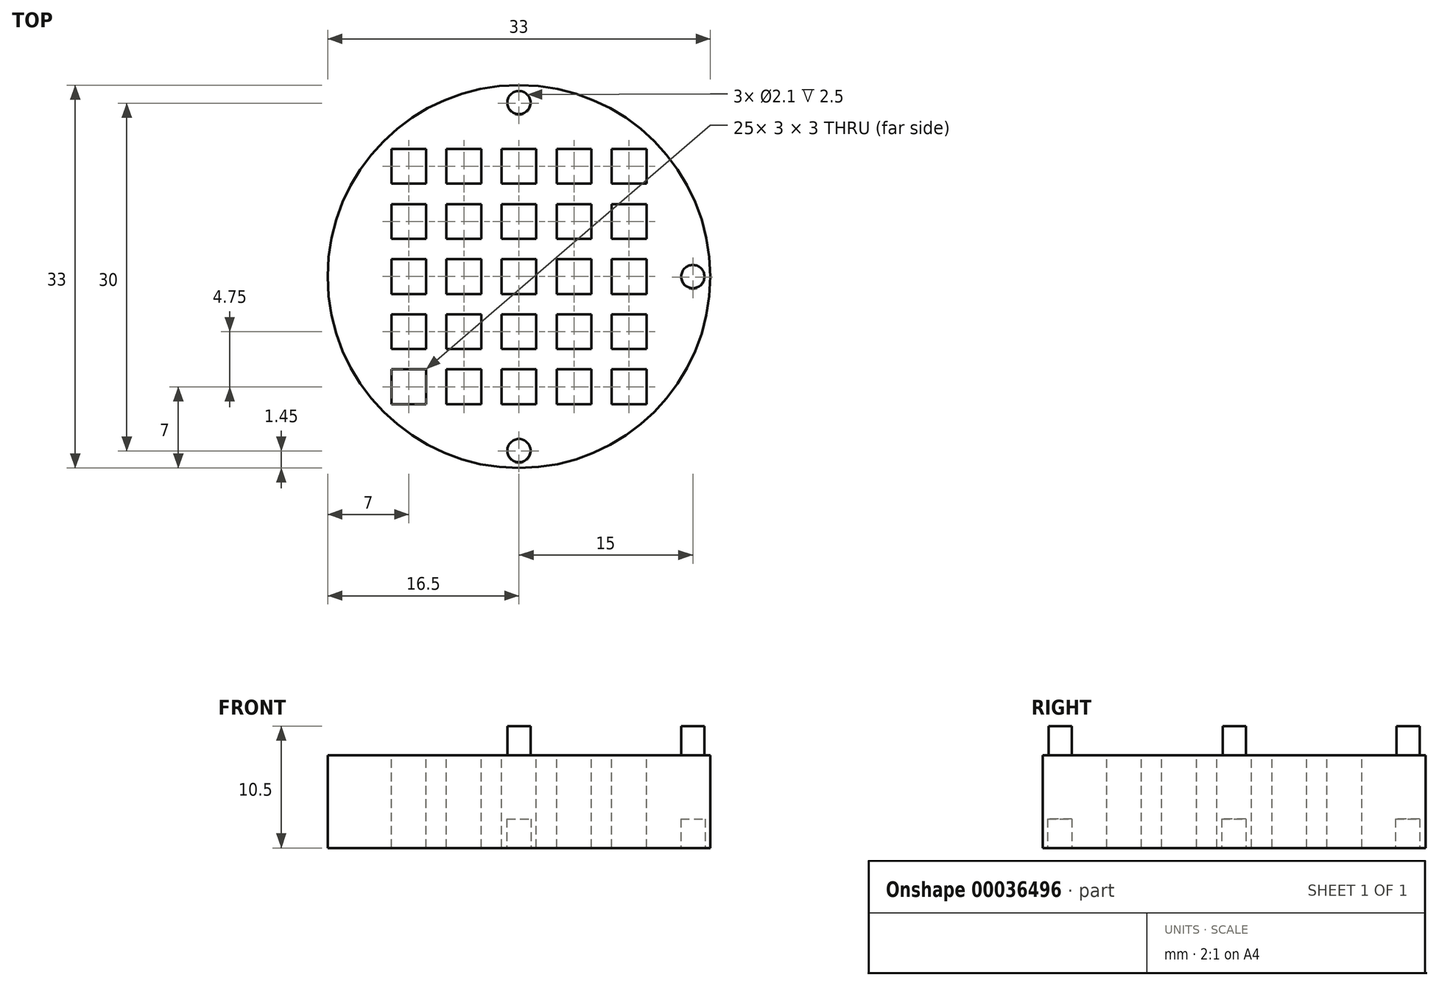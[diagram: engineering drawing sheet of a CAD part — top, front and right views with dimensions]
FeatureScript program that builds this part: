
annotation { "Feature Type Name" : "Feature", "Feature Type Description" : "" }
export const myFeature = defineFeature(function(context is Context, id is Id, definition is map)
    precondition{}
    {
        {
            var Q0;
            Q0=qCreatedBy(makeId("Top.planeOp"),FACE);
            var sketch = newSketch(context, id + "F0", { "sketchPlane" : qUnion([Q0])});
            skCircle(sketch, "E0", {"center": v(0, 0) * mm, "radius": 16.5 * mm});
            skSolve(sketch);
        }
        {
            var Q0;
            Q0=qSketchRegion(id+"F0",true);
            extrude(context, id + "F1", {"entities" : qUnion([Q0]), "depth" : 8 * mm});
        }
        {
            var Q0;
            Q0=makeQuery(id+"F1.opExtrude","CAP_FACE",FACE,{"disambiguationData":[OSD([sQuery(id+"F0.wireOp",EDGE,"E0")])],"isStart":true});
            var sketch = newSketch(context, id + "F2", { "sketchPlane" : qUnion([Q0])});
            skCircle(sketch, "E1", {"center": v(0, 15.05) * mm, "radius": 1.05 * mm});
            skCircle(sketch, "E2.1.0", {"center": v(15, 0.05) * mm, "radius": 1.05 * mm});
            skCircle(sketch, "E2.2.0", {"center": v(0, -14.95) * mm, "radius": 1.05 * mm});
            skPoint(sketch, "E2.center", {"position": v(0, 0.05) * mm});
            skLineSegment(sketch, "E2.anchor1", {"start": v(0, 0.05) * mm, "end": v(0, 15.05) * mm, "construction": true});
            skLineSegment(sketch, "E2.anchor2", {"start": v(0, 0.05) * mm, "end": v(0, -14.95) * mm, "construction": true});
            skSolve(sketch);
        }
        {
            var Q0;
            Q0=qSketchRegion(id+"F2",true);
            extrude(context, id + "F3", {"entities" : qUnion([Q0]), "operationType" : NewBodyOperationType.REMOVE, "oppositeDirection" : true, "depth" : 2.5 * mm});
        }
        {
            var Q0;
            Q0=makeQuery(id+"F1.opExtrude","CAP_FACE",FACE,{"disambiguationData":[OSD([sQuery(id+"F0.wireOp",EDGE,"E0")])],"isStart":false});
            var sketch = newSketch(context, id + "F4", { "sketchPlane" : qUnion([Q0])});
            skCircle(sketch, "E3", {"center": v(0, 15) * mm, "radius": 1 * mm});
            skCircle(sketch, "E4.1.0", {"center": v(15, 0) * mm, "radius": 1 * mm});
            skCircle(sketch, "E4.2.0", {"center": v(0, -15) * mm, "radius": 1 * mm});
            skPoint(sketch, "E4.center", {"position": v(0, 0) * mm});
            skLineSegment(sketch, "E4.anchor1", {"start": v(0, 0) * mm, "end": v(0, 15) * mm, "construction": true});
            skLineSegment(sketch, "E4.anchor2", {"start": v(0, 0) * mm, "end": v(0, -15) * mm, "construction": true});
            skSolve(sketch);
        }
        {
            var Q0;
            Q0=qSketchRegion(id+"F4",true);
            extrude(context, id + "F5", {"entities" : qUnion([Q0]), "operationType" : NewBodyOperationType.ADD, "depth" : 2.5 * mm});
        }
        {
            var Q0;
            Q0=makeQuery(id+"F1.opExtrude","CAP_FACE",FACE,{"disambiguationData":[OSD([sQuery(id+"F0.wireOp",EDGE,"E0")])],"isStart":false});
            var sketch = newSketch(context, id + "F6", { "sketchPlane" : qUnion([Q0])});
            skLineSegment(sketch, "E5.bottom", {"start": v(-11, 11) * mm, "end": v(-8, 11) * mm});
            skLineSegment(sketch, "E5.top", {"start": v(-11, 8) * mm, "end": v(-8, 8) * mm});
            skLineSegment(sketch, "E5.left", {"start": v(-11, 11) * mm, "end": v(-11, 8) * mm});
            skLineSegment(sketch, "E5.right", {"start": v(-8, 11) * mm, "end": v(-8, 8) * mm});
            skLineSegment(sketch, "E6.0.1.0", {"start": v(-11, 6.25) * mm, "end": v(-8, 6.25) * mm});
            skLineSegment(sketch, "E6.0.1.1", {"start": v(-11, 6.25) * mm, "end": v(-11, 3.25) * mm});
            skLineSegment(sketch, "E6.0.1.2", {"start": v(-8, 6.25) * mm, "end": v(-8, 3.25) * mm});
            skLineSegment(sketch, "E6.0.1.3", {"start": v(-11, 3.25) * mm, "end": v(-8, 3.25) * mm});
            skLineSegment(sketch, "E6.0.2.0", {"start": v(-11, 1.5) * mm, "end": v(-8, 1.5) * mm});
            skLineSegment(sketch, "E6.0.2.1", {"start": v(-11, 1.5) * mm, "end": v(-11, -1.5) * mm});
            skLineSegment(sketch, "E6.0.2.2", {"start": v(-8, 1.5) * mm, "end": v(-8, -1.5) * mm});
            skLineSegment(sketch, "E6.0.2.3", {"start": v(-11, -1.5) * mm, "end": v(-8, -1.5) * mm});
            skLineSegment(sketch, "E6.0.3.0", {"start": v(-11, -3.25) * mm, "end": v(-8, -3.25) * mm});
            skLineSegment(sketch, "E6.0.3.1", {"start": v(-11, -3.25) * mm, "end": v(-11, -6.25) * mm});
            skLineSegment(sketch, "E6.0.3.2", {"start": v(-8, -3.25) * mm, "end": v(-8, -6.25) * mm});
            skLineSegment(sketch, "E6.0.3.3", {"start": v(-11, -6.25) * mm, "end": v(-8, -6.25) * mm});
            skLineSegment(sketch, "E6.0.4.0", {"start": v(-11, -8) * mm, "end": v(-8, -8) * mm});
            skLineSegment(sketch, "E6.0.4.1", {"start": v(-11, -8) * mm, "end": v(-11, -11) * mm});
            skLineSegment(sketch, "E6.0.4.2", {"start": v(-8, -8) * mm, "end": v(-8, -11) * mm});
            skLineSegment(sketch, "E6.0.4.3", {"start": v(-11, -11) * mm, "end": v(-8, -11) * mm});
            skLineSegment(sketch, "E6.1.0.0", {"start": v(-6.25, 11) * mm, "end": v(-3.25, 11) * mm});
            skLineSegment(sketch, "E6.1.0.1", {"start": v(-6.25, 11) * mm, "end": v(-6.25, 8) * mm});
            skLineSegment(sketch, "E6.1.0.2", {"start": v(-3.25, 11) * mm, "end": v(-3.25, 8) * mm});
            skLineSegment(sketch, "E6.1.0.3", {"start": v(-6.25, 8) * mm, "end": v(-3.25, 8) * mm});
            skLineSegment(sketch, "E6.1.1.0", {"start": v(-6.25, 6.25) * mm, "end": v(-3.25, 6.25) * mm});
            skLineSegment(sketch, "E6.1.1.1", {"start": v(-6.25, 6.25) * mm, "end": v(-6.25, 3.25) * mm});
            skLineSegment(sketch, "E6.1.1.2", {"start": v(-3.25, 6.25) * mm, "end": v(-3.25, 3.25) * mm});
            skLineSegment(sketch, "E6.1.1.3", {"start": v(-6.25, 3.25) * mm, "end": v(-3.25, 3.25) * mm});
            skLineSegment(sketch, "E6.1.2.0", {"start": v(-6.25, 1.5) * mm, "end": v(-3.25, 1.5) * mm});
            skLineSegment(sketch, "E6.1.2.1", {"start": v(-6.25, 1.5) * mm, "end": v(-6.25, -1.5) * mm});
            skLineSegment(sketch, "E6.1.2.2", {"start": v(-3.25, 1.5) * mm, "end": v(-3.25, -1.5) * mm});
            skLineSegment(sketch, "E6.1.2.3", {"start": v(-6.25, -1.5) * mm, "end": v(-3.25, -1.5) * mm});
            skLineSegment(sketch, "E6.1.3.0", {"start": v(-6.25, -3.25) * mm, "end": v(-3.25, -3.25) * mm});
            skLineSegment(sketch, "E6.1.3.1", {"start": v(-6.25, -3.25) * mm, "end": v(-6.25, -6.25) * mm});
            skLineSegment(sketch, "E6.1.3.2", {"start": v(-3.25, -3.25) * mm, "end": v(-3.25, -6.25) * mm});
            skLineSegment(sketch, "E6.1.3.3", {"start": v(-6.25, -6.25) * mm, "end": v(-3.25, -6.25) * mm});
            skLineSegment(sketch, "E6.1.4.0", {"start": v(-6.25, -8) * mm, "end": v(-3.25, -8) * mm});
            skLineSegment(sketch, "E6.1.4.1", {"start": v(-6.25, -8) * mm, "end": v(-6.25, -11) * mm});
            skLineSegment(sketch, "E6.1.4.2", {"start": v(-3.25, -8) * mm, "end": v(-3.25, -11) * mm});
            skLineSegment(sketch, "E6.1.4.3", {"start": v(-6.25, -11) * mm, "end": v(-3.25, -11) * mm});
            skLineSegment(sketch, "E6.2.0.0", {"start": v(-1.5, 11) * mm, "end": v(1.5, 11) * mm});
            skLineSegment(sketch, "E6.2.0.1", {"start": v(-1.5, 11) * mm, "end": v(-1.5, 8) * mm});
            skLineSegment(sketch, "E6.2.0.2", {"start": v(1.5, 11) * mm, "end": v(1.5, 8) * mm});
            skLineSegment(sketch, "E6.2.0.3", {"start": v(-1.5, 8) * mm, "end": v(1.5, 8) * mm});
            skLineSegment(sketch, "E6.2.1.0", {"start": v(-1.5, 6.25) * mm, "end": v(1.5, 6.25) * mm});
            skLineSegment(sketch, "E6.2.1.1", {"start": v(-1.5, 6.25) * mm, "end": v(-1.5, 3.25) * mm});
            skLineSegment(sketch, "E6.2.1.2", {"start": v(1.5, 6.25) * mm, "end": v(1.5, 3.25) * mm});
            skLineSegment(sketch, "E6.2.1.3", {"start": v(-1.5, 3.25) * mm, "end": v(1.5, 3.25) * mm});
            skLineSegment(sketch, "E6.2.2.0", {"start": v(-1.5, 1.5) * mm, "end": v(1.5, 1.5) * mm});
            skLineSegment(sketch, "E6.2.2.1", {"start": v(-1.5, 1.5) * mm, "end": v(-1.5, -1.5) * mm});
            skLineSegment(sketch, "E6.2.2.2", {"start": v(1.5, 1.5) * mm, "end": v(1.5, -1.5) * mm});
            skLineSegment(sketch, "E6.2.2.3", {"start": v(-1.5, -1.5) * mm, "end": v(1.5, -1.5) * mm});
            skLineSegment(sketch, "E6.2.3.0", {"start": v(-1.5, -3.25) * mm, "end": v(1.5, -3.25) * mm});
            skLineSegment(sketch, "E6.2.3.1", {"start": v(-1.5, -3.25) * mm, "end": v(-1.5, -6.25) * mm});
            skLineSegment(sketch, "E6.2.3.2", {"start": v(1.5, -3.25) * mm, "end": v(1.5, -6.25) * mm});
            skLineSegment(sketch, "E6.2.3.3", {"start": v(-1.5, -6.25) * mm, "end": v(1.5, -6.25) * mm});
            skLineSegment(sketch, "E6.2.4.0", {"start": v(-1.5, -8) * mm, "end": v(1.5, -8) * mm});
            skLineSegment(sketch, "E6.2.4.1", {"start": v(-1.5, -8) * mm, "end": v(-1.5, -11) * mm});
            skLineSegment(sketch, "E6.2.4.2", {"start": v(1.5, -8) * mm, "end": v(1.5, -11) * mm});
            skLineSegment(sketch, "E6.2.4.3", {"start": v(-1.5, -11) * mm, "end": v(1.5, -11) * mm});
            skLineSegment(sketch, "E6.3.0.0", {"start": v(3.25, 11) * mm, "end": v(6.25, 11) * mm});
            skLineSegment(sketch, "E6.3.0.1", {"start": v(3.25, 11) * mm, "end": v(3.25, 8) * mm});
            skLineSegment(sketch, "E6.3.0.2", {"start": v(6.25, 11) * mm, "end": v(6.25, 8) * mm});
            skLineSegment(sketch, "E6.3.0.3", {"start": v(3.25, 8) * mm, "end": v(6.25, 8) * mm});
            skLineSegment(sketch, "E6.3.1.0", {"start": v(3.25, 6.25) * mm, "end": v(6.25, 6.25) * mm});
            skLineSegment(sketch, "E6.3.1.1", {"start": v(3.25, 6.25) * mm, "end": v(3.25, 3.25) * mm});
            skLineSegment(sketch, "E6.3.1.2", {"start": v(6.25, 6.25) * mm, "end": v(6.25, 3.25) * mm});
            skLineSegment(sketch, "E6.3.1.3", {"start": v(3.25, 3.25) * mm, "end": v(6.25, 3.25) * mm});
            skLineSegment(sketch, "E6.3.2.0", {"start": v(3.25, 1.5) * mm, "end": v(6.25, 1.5) * mm});
            skLineSegment(sketch, "E6.3.2.1", {"start": v(3.25, 1.5) * mm, "end": v(3.25, -1.5) * mm});
            skLineSegment(sketch, "E6.3.2.2", {"start": v(6.25, 1.5) * mm, "end": v(6.25, -1.5) * mm});
            skLineSegment(sketch, "E6.3.2.3", {"start": v(3.25, -1.5) * mm, "end": v(6.25, -1.5) * mm});
            skLineSegment(sketch, "E6.3.3.0", {"start": v(3.25, -3.25) * mm, "end": v(6.25, -3.25) * mm});
            skLineSegment(sketch, "E6.3.3.1", {"start": v(3.25, -3.25) * mm, "end": v(3.25, -6.25) * mm});
            skLineSegment(sketch, "E6.3.3.2", {"start": v(6.25, -3.25) * mm, "end": v(6.25, -6.25) * mm});
            skLineSegment(sketch, "E6.3.3.3", {"start": v(3.25, -6.25) * mm, "end": v(6.25, -6.25) * mm});
            skLineSegment(sketch, "E6.3.4.0", {"start": v(3.25, -8) * mm, "end": v(6.25, -8) * mm});
            skLineSegment(sketch, "E6.3.4.1", {"start": v(3.25, -8) * mm, "end": v(3.25, -11) * mm});
            skLineSegment(sketch, "E6.3.4.2", {"start": v(6.25, -8) * mm, "end": v(6.25, -11) * mm});
            skLineSegment(sketch, "E6.3.4.3", {"start": v(3.25, -11) * mm, "end": v(6.25, -11) * mm});
            skLineSegment(sketch, "E6.4.0.0", {"start": v(8, 11) * mm, "end": v(11, 11) * mm});
            skLineSegment(sketch, "E6.4.0.1", {"start": v(8, 11) * mm, "end": v(8, 8) * mm});
            skLineSegment(sketch, "E6.4.0.2", {"start": v(11, 11) * mm, "end": v(11, 8) * mm});
            skLineSegment(sketch, "E6.4.0.3", {"start": v(8, 8) * mm, "end": v(11, 8) * mm});
            skLineSegment(sketch, "E6.4.1.0", {"start": v(8, 6.25) * mm, "end": v(11, 6.25) * mm});
            skLineSegment(sketch, "E6.4.1.1", {"start": v(8, 6.25) * mm, "end": v(8, 3.25) * mm});
            skLineSegment(sketch, "E6.4.1.2", {"start": v(11, 6.25) * mm, "end": v(11, 3.25) * mm});
            skLineSegment(sketch, "E6.4.1.3", {"start": v(8, 3.25) * mm, "end": v(11, 3.25) * mm});
            skLineSegment(sketch, "E6.4.2.0", {"start": v(8, 1.5) * mm, "end": v(11, 1.5) * mm});
            skLineSegment(sketch, "E6.4.2.1", {"start": v(8, 1.5) * mm, "end": v(8, -1.5) * mm});
            skLineSegment(sketch, "E6.4.2.2", {"start": v(11, 1.5) * mm, "end": v(11, -1.5) * mm});
            skLineSegment(sketch, "E6.4.2.3", {"start": v(8, -1.5) * mm, "end": v(11, -1.5) * mm});
            skLineSegment(sketch, "E6.4.3.0", {"start": v(8, -3.25) * mm, "end": v(11, -3.25) * mm});
            skLineSegment(sketch, "E6.4.3.1", {"start": v(8, -3.25) * mm, "end": v(8, -6.25) * mm});
            skLineSegment(sketch, "E6.4.3.2", {"start": v(11, -3.25) * mm, "end": v(11, -6.25) * mm});
            skLineSegment(sketch, "E6.4.3.3", {"start": v(8, -6.25) * mm, "end": v(11, -6.25) * mm});
            skLineSegment(sketch, "E6.4.4.0", {"start": v(8, -8) * mm, "end": v(11, -8) * mm});
            skLineSegment(sketch, "E6.4.4.1", {"start": v(8, -8) * mm, "end": v(8, -11) * mm});
            skLineSegment(sketch, "E6.4.4.2", {"start": v(11, -8) * mm, "end": v(11, -11) * mm});
            skLineSegment(sketch, "E6.4.4.3", {"start": v(8, -11) * mm, "end": v(11, -11) * mm});
            skLineSegment(sketch, "E6.direction1", {"start": v(-11, 11) * mm, "end": v(-6.25, 11) * mm, "construction": true});
            skLineSegment(sketch, "E6.direction2", {"start": v(-11, 11) * mm, "end": v(-11, 6.25) * mm, "construction": true});
            skSolve(sketch);
        }
        {
            var Q0;
            Q0 = qSketchRegion(id + "F6", true);
            extrude(context, id + "F7", {"entities" : qUnion([Q0]), "operationType" : NewBodyOperationType.REMOVE, "endBound" : BoundingType.THROUGH_ALL, "oppositeDirection" : true, "depth" : 25 * mm});
        }
    });
